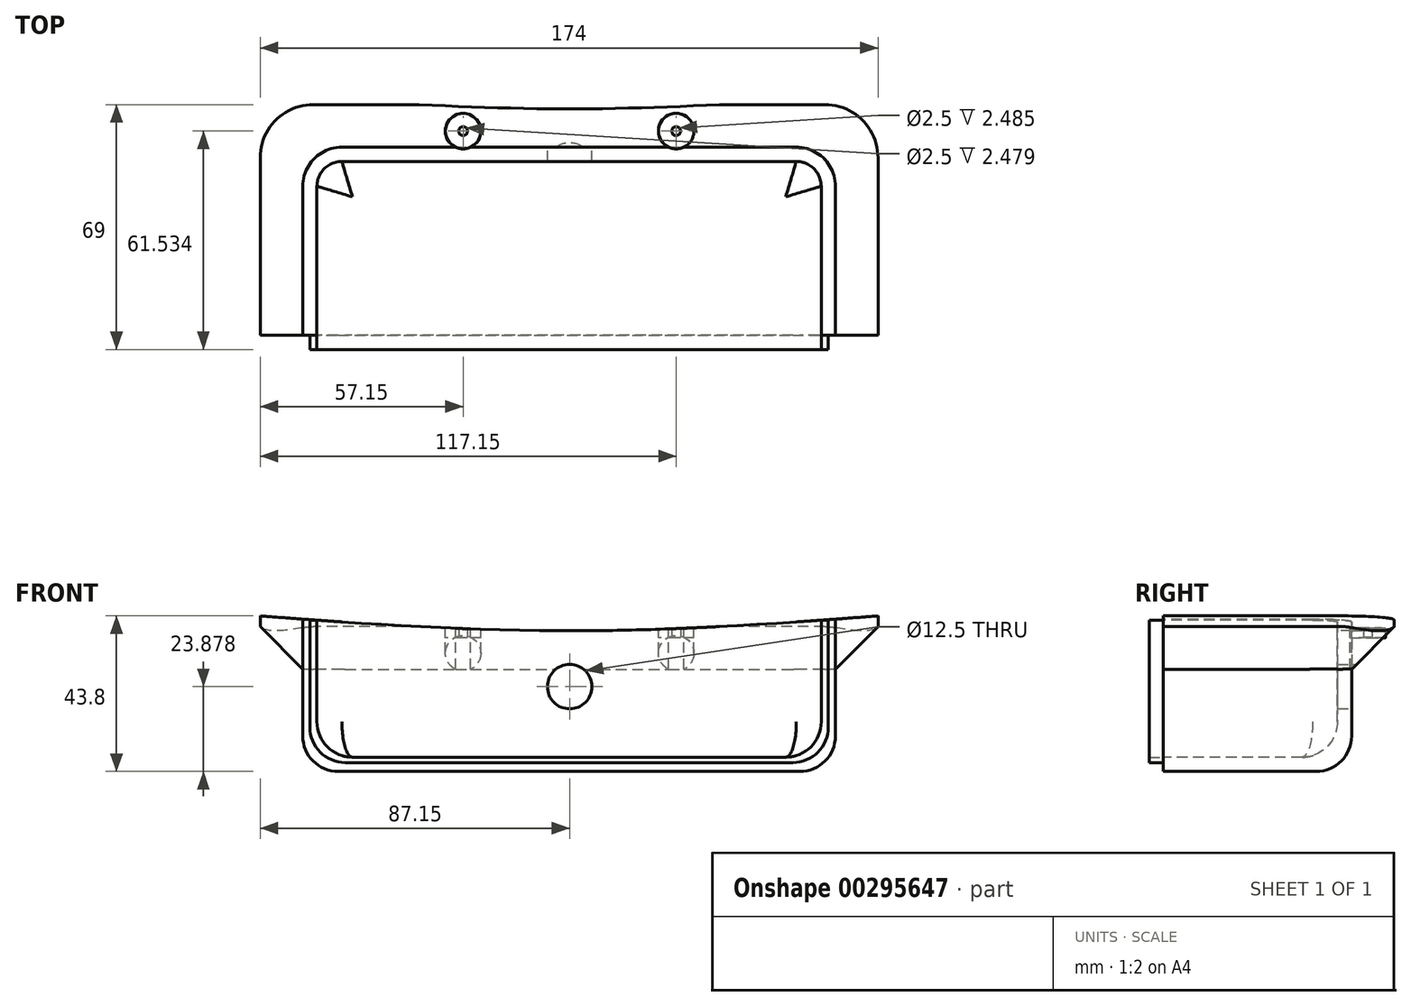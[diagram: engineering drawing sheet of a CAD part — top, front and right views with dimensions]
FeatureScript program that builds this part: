
annotation { "Feature Type Name" : "Feature", "Feature Type Description" : "" }
export const myFeature = defineFeature(function(context is Context, id is Id, definition is map)
    precondition{}
    {
        {
            var Q0;
            Q0=qCreatedBy(makeId("Top.planeOp"),FACE);
            var sketch = newSketch(context, id + "F0", { "sketchPlane" : qUnion([Q0])});
            skLineSegment(sketch, "E0.bottom", {"start": v(-64.15, 90.67) * mm, "end": v(63.85, 90.67) * mm});
            skLineSegment(sketch, "E0.top", {"start": v(-75.15, 37.67) * mm, "end": v(74.85, 37.67) * mm});
            skLineSegment(sketch, "E0.left", {"start": v(-75.15, 79.67) * mm, "end": v(-75.15, 37.67) * mm});
            skLineSegment(sketch, "E0.right", {"start": v(74.85, 79.67) * mm, "end": v(74.85, 37.67) * mm});
            skPoint(sketch, "E1.visualSharp", {"position": v(-75.15, 90.67) * mm});
            skArc(sketch, "E1.filletArc", {"start": v(-64.15, 90.67) * mm, "mid": v(-71.93, 87.45) * mm, "end": v(-75.15, 79.67) * mm});
            skPoint(sketch, "E2.visualSharp", {"position": v(74.85, 90.67) * mm});
            skArc(sketch, "E2.filletArc", {"start": v(74.85, 79.67) * mm, "mid": v(71.62, 87.45) * mm, "end": v(63.85, 90.67) * mm});
            skSolve(sketch);
        }
        {
            var Q0;
            Q0=qSketchRegion(id+"F0",true);
            extrude(context, id + "F1", {"entities" : qUnion([Q0]), "depth" : 43.8 * mm, "offsetDistance" : 25 * mm});
        }
        {
            var Q0;
            Q0=makeQuery(id+"F1.opExtrude","CAP_FACE",FACE,{"disambiguationData":[OSD([sQuery(id+"F0.wireOp",EDGE,"E0.bottom"),sQuery(id+"F0.wireOp",EDGE,"E0.top"),sQuery(id+"F0.wireOp",EDGE,"E0.left"),sQuery(id+"F0.wireOp",EDGE,"E0.right")])],"isStart":false});
            shell(context, id + "F2", {"entities" : qUnion([Q0]), "thickness" : 4 * mm});
        }
        {
            var Q0;
            Q0=makeQuery(id+"F1.opExtrude","CAP_FACE",FACE,{"disambiguationData":[OSD([sQuery(id+"F0.wireOp",EDGE,"E0.bottom"),sQuery(id+"F0.wireOp",EDGE,"E0.top"),sQuery(id+"F0.wireOp",EDGE,"E0.left"),sQuery(id+"F0.wireOp",EDGE,"E0.right"),sQuery(id+"F0.wireOp",EDGE,"E1.filletArc"),sQuery(id+"F0.wireOp",EDGE,"E2.filletArc")])],"isStart":false});
            var sketch = newSketch(context, id + "F3", { "sketchPlane" : qUnion([Q0])});
            skLineSegment(sketch, "E3.bottom", {"start": v(-71.15, 41.67) * mm, "end": v(70.85, 41.67) * mm});
            skLineSegment(sketch, "E3.top", {"start": v(-71.15, 37.67) * mm, "end": v(70.85, 37.67) * mm});
            skLineSegment(sketch, "E3.left", {"start": v(-71.15, 41.67) * mm, "end": v(-71.15, 37.67) * mm});
            skLineSegment(sketch, "E3.right", {"start": v(70.85, 41.67) * mm, "end": v(70.85, 37.67) * mm});
            skSolve(sketch);
        }
        {
            var Q0;
            Q0=qSketchRegion(id+"F3",true);
            extrude(context, id + "F4", {"entities" : qUnion([Q0]), "operationType" : NewBodyOperationType.REMOVE, "oppositeDirection" : true, "depth" : 39.8 * mm, "offsetDistance" : 25 * mm});
        }
        {
            var Q0;
            Q0=makeQuery(id+"FrwUbtnxUC9HyyJ_1.boolean.opBoolean","MERGE",FACE,{"derivedFrom":[makeQuery(id+"F1.opExtrude","CAP_FACE",FACE,{"disambiguationData":[OSD([sQuery(id+"F0.wireOp",EDGE,"E0.bottom"),sQuery(id+"F0.wireOp",EDGE,"E0.top"),sQuery(id+"F0.wireOp",EDGE,"E0.left"),sQuery(id+"F0.wireOp",EDGE,"E0.right"),sQuery(id+"F0.wireOp",EDGE,"E1.filletArc"),sQuery(id+"F0.wireOp",EDGE,"E2.filletArc")])],"isStart":false}),makeQuery(id+"FrwUbtnxUC9HyyJ_1.opExtrude","CAP_FACE",FACE,{"disambiguationData":[OSD([sQuery(id+"FibHU4dr98Ndzw2_1.wireOp",EDGE,"9rjzK8EU-co4c-AKP1-GJnL-XDDrkJgZbtAS.bottom"),sQuery(id+"FibHU4dr98Ndzw2_1.wireOp",EDGE,"9rjzK8EU-co4c-AKP1-GJnL-XDDrkJgZbtAS.top"),sQuery(id+"FibHU4dr98Ndzw2_1.wireOp",EDGE,"9rjzK8EU-co4c-AKP1-GJnL-XDDrkJgZbtAS.left"),sQuery(id+"FibHU4dr98Ndzw2_1.wireOp",EDGE,"9rjzK8EU-co4c-AKP1-GJnL-XDDrkJgZbtAS.right")])],"isStart":true})]});
            var sketch = newSketch(context, id + "F5", { "sketchPlane" : qUnion([Q0])});
            skLineSegment(sketch, "E4.top", {"start": v(74.85, 37.67) * mm, "end": v(86.85, 37.67) * mm});
            skPoint(sketch, "E5.visualSharp", {"position": v(86.85, 102.67) * mm});
            skLineSegment(sketch, "E6", {"start": v(86.85, 102.67) * mm, "end": v(86.85, 37.67) * mm});
            skLineSegment(sketch, "E7.bottom", {"start": v(-75.15, 37.67) * mm, "end": v(-87.15, 37.67) * mm});
            skLineSegment(sketch, "E8", {"start": v(86.85, 102.67) * mm, "end": v(-87.15, 102.67) * mm});
            skLineSegment(sketch, "E9", {"start": v(-87.15, 102.67) * mm, "end": v(-87.15, 37.67) * mm});
            skLineSegment(sketch, "E10", {"start": v(-75.15, 37.67) * mm, "end": v(-75.15, 79.67) * mm});
            skLineSegment(sketch, "E11", {"start": v(-75.15, 79.67) * mm, "end": v(-75.15, 79.67) * mm});
            skLineSegment(sketch, "E12", {"start": v(-64.15, 90.67) * mm, "end": v(-64.15, 90.67) * mm});
            skLineSegment(sketch, "E13", {"start": v(-64.15, 90.67) * mm, "end": v(63.85, 90.67) * mm});
            skLineSegment(sketch, "E14", {"start": v(63.85, 90.67) * mm, "end": v(63.85, 90.67) * mm});
            skLineSegment(sketch, "E15", {"start": v(74.85, 79.67) * mm, "end": v(74.85, 79.67) * mm});
            skLineSegment(sketch, "E16", {"start": v(74.85, 79.67) * mm, "end": v(74.85, 37.67) * mm});
            skPoint(sketch, "E17.visualSharp", {"position": v(-75.15, 90.67) * mm});
            skArc(sketch, "E17.filletArc", {"start": v(-64.15, 90.67) * mm, "mid": v(-71.93, 87.45) * mm, "end": v(-75.15, 79.67) * mm});
            skPoint(sketch, "E18.visualSharp", {"position": v(74.85, 90.67) * mm});
            skArc(sketch, "E18.filletArc", {"start": v(74.85, 79.67) * mm, "mid": v(71.62, 87.45) * mm, "end": v(63.85, 90.67) * mm});
            skSolve(sketch);
        }
        {
            var Q0;
            Q0=qSketchRegion(id+"F5",true);
            extrude(context, id + "F6", {"entities" : qUnion([Q0]), "oppositeDirection" : true, "depth" : 15 * mm});
        }
        {
            var Q0;
            Q0=makeQuery(id+"F6.opExtrude","CAP_EDGE",EDGE,{"disambiguationData":[OSD([sQuery(id+"F5.wireOp",EDGE,"OsvB9Zjt-Pbkl-vpw5-N01A-Guk8HrNlOFjG")])],"isStart":false});
            var Q1;
            Q1=makeQuery(id+"F6.opExtrude","CAP_EDGE",EDGE,{"disambiguationData":[OSD([sQuery(id+"F5.wireOp",EDGE,"jzA2utPZ-bsNO-buFr-XQbU-ETDa1rF8MsZR")])],"isStart":false});
            var Q2;
            Q2=makeQuery(id+"F6.opExtrude","CAP_EDGE",EDGE,{"disambiguationData":[OSD([sQuery(id+"F5.wireOp",EDGE,"E6")])],"isStart":false});
            var Q3;
            Q3=makeQuery(id+"F6.opExtrude","CAP_EDGE",EDGE,{"disambiguationData":[OSD([sQuery(id+"F5.wireOp",EDGE,"ZfQyCJF3-zcwV-7PIL-13Iy-nZyDA9thB6iG")])],"isStart":false});
            var Q4;
            Q4=makeQuery(id+"F6.opExtrude","CAP_EDGE",EDGE,{"disambiguationData":[OSD([sQuery(id+"F5.wireOp",EDGE,"E8")])],"isStart":false});
            var Q5;
            Q5=makeQuery(id+"F6.opExtrude","CAP_EDGE",EDGE,{"disambiguationData":[OSD([sQuery(id+"F5.wireOp",EDGE,"E9")])],"isStart":false});
            chamfer(context, id + "F7", {"entities" : qUnion([Q0, Q1, Q2, Q3, Q4, Q5]), "width" : 12 * mm, "tangentPropagation" : true});
        }
        {
            var Q0;
            Q0=makeQuery(id+"F6.opExtrude","SWEPT_EDGE",EDGE,{"disambiguationData":[OSD([sQuery(id+"F5.wireOp",EDGE,"E8"),sQuery(id+"F5.wireOp",EDGE,"E9")])]});
            var Q1;
            Q1=makeQuery(id+"F6.opExtrude","SWEPT_EDGE",EDGE,{"disambiguationData":[OSD([sQuery(id+"F5.wireOp",EDGE,"E6"),sQuery(id+"F5.wireOp",EDGE,"E8")])]});
            fillet(context, id + "F8", {"entities" : qUnion([Q0, Q1]), "radius" : 15 * mm, "tangentPropagation" : true, "allowEdgeOverflow" : false});
        }
        {
            var Q0;
            Q0=makeQuery(id+"F7.opChamfer","BLEND_EDGE",EDGE,{"blendedFrom":[makeQuery(id+"F6.opExtrude","CAP_EDGE",EDGE,{"disambiguationData":[OSD([sQuery(id+"F5.wireOp",EDGE,"E6")])],"isStart":false}),makeQuery(id+"F6.opExtrude","CAP_EDGE",EDGE,{"disambiguationData":[OSD([sQuery(id+"F5.wireOp",EDGE,"E8")])],"isStart":false})],"blendedInto":[]});
            var Q1;
            Q1=makeQuery(id+"F7.opChamfer","BLEND_EDGE",EDGE,{"blendedFrom":[makeQuery(id+"F6.opExtrude","CAP_EDGE",EDGE,{"disambiguationData":[OSD([sQuery(id+"F5.wireOp",EDGE,"E8")])],"isStart":false}),makeQuery(id+"F6.opExtrude","CAP_EDGE",EDGE,{"disambiguationData":[OSD([sQuery(id+"F5.wireOp",EDGE,"E9")])],"isStart":false})],"blendedInto":[]});
            fillet(context, id + "F9", {"entities" : qUnion([Q0, Q1]), "radius" : 17 * mm, "tangentPropagation" : true, "allowEdgeOverflow" : false});
        }
        {
            var Q0;
            {var subQ0=sQuery(id+"F5.wireOp",EDGE,"E13");var subQ1=sQuery(id+"F5.wireOp",EDGE,"E8");var subQ2=sQuery(id+"F5.wireOp",EDGE,"E6");var subQ3=sQuery(id+"F5.wireOp",EDGE,"E4.top");var subQ4=sQuery(id+"F5.wireOp",EDGE,"E18.filletArc");var subQ5=sQuery(id+"F5.wireOp",EDGE,"E16");Q0=makeQuery(id+"FgmOIsl14va52HR_2.boolean.opBoolean","SPLIT",FACE,{"disambiguationData":[TD([makeQuery(id+"F6.opExtrude","SWEPT_FACE",FACE,{"disambiguationData":[OSD([subQ3])]})])],"derivedFrom":makeQuery(id+"Fe1wAfX2hFDYVoF_2.boolean.opBoolean","MERGE",FACE,{"derivedFrom":[makeQuery(id+"F6.opExtrude","CAP_FACE",FACE,{"disambiguationData":[OSD([subQ3,subQ2,sQuery(id+"F5.wireOp",EDGE,"E7.bottom"),subQ1,sQuery(id+"F5.wireOp",EDGE,"E9"),sQuery(id+"F5.wireOp",EDGE,"E10"),subQ0,subQ5,sQuery(id+"F5.wireOp",EDGE,"E17.filletArc"),subQ4])],"isStart":true}),makeQuery(id+"Fe1wAfX2hFDYVoF_2.opExtrude","CAP_FACE",FACE,{"disambiguationData":[OSD([sQuery(id+"Fb9MMb573N5PaO1_2.wireOp",EDGE,"NLJTObmN-SUbK-zKRp-w8bl-v2nN1BY6rHCR")])],"isStart":true}),makeQuery(id+"Fe1wAfX2hFDYVoF_2.opExtrude","CAP_FACE",FACE,{"disambiguationData":[OSD([sQuery(id+"Fb9MMb573N5PaO1_2.wireOp",EDGE,"s3ml98qp-wij4-XS56-vTp4-YSEt5g6wRKUZ")])],"isStart":true}),makeQuery(id+"Fe1wAfX2hFDYVoF_2.opExtrude","CAP_FACE",FACE,{"disambiguationData":[OSD([sQuery(id+"Fb9MMb573N5PaO1_2.wireOp",EDGE,"b1kLfqmR-9x7Y-TcUW-Umgw-XTBiy1vxkqET")])],"isStart":true}),makeQuery(id+"Fe1wAfX2hFDYVoF_2.opExtrude","CAP_FACE",FACE,{"disambiguationData":[OSD([sQuery(id+"Fb9MMb573N5PaO1_2.wireOp",EDGE,"wZv8IqiW-lJnz-yde2-UiWY-uM58CcvMkqUG")])],"isStart":true})]})});}
            var sketch = newSketch(context, id + "F10", { "sketchPlane" : qUnion([Q0])});
            skCircle(sketch, "E19", {"center": v(30, 95.2) * mm, "radius": 5 * mm});
            skCircle(sketch, "E20", {"center": v(-30, 95.2) * mm, "radius": 5 * mm});
            skSolve(sketch);
        }
        {
            var Q0;
            Q0=qSketchRegion(id+"F10",true);
            extrude(context, id + "F11", {"entities" : qUnion([Q0]), "operationType" : NewBodyOperationType.REMOVE, "oppositeDirection" : true, "depth" : 15 * mm});
        }
        {
            var Q0;
            {var subQ0=sQuery(id+"F5.wireOp",EDGE,"E13");var subQ1=sQuery(id+"F5.wireOp",EDGE,"E8");var subQ2=sQuery(id+"F5.wireOp",EDGE,"E6");var subQ3=sQuery(id+"F5.wireOp",EDGE,"E4.top");var subQ4=sQuery(id+"F5.wireOp",EDGE,"E18.filletArc");var subQ5=sQuery(id+"F5.wireOp",EDGE,"E16");Q0=makeQuery(id+"FgmOIsl14va52HR_2.boolean.opBoolean","SPLIT",FACE,{"disambiguationData":[TD([makeQuery(id+"F6.opExtrude","SWEPT_FACE",FACE,{"disambiguationData":[OSD([subQ3])]})])],"derivedFrom":makeQuery(id+"Fe1wAfX2hFDYVoF_2.boolean.opBoolean","MERGE",FACE,{"derivedFrom":[makeQuery(id+"F6.opExtrude","CAP_FACE",FACE,{"disambiguationData":[OSD([subQ3,subQ2,sQuery(id+"F5.wireOp",EDGE,"E7.bottom"),subQ1,sQuery(id+"F5.wireOp",EDGE,"E9"),sQuery(id+"F5.wireOp",EDGE,"E10"),subQ0,subQ5,sQuery(id+"F5.wireOp",EDGE,"E17.filletArc"),subQ4])],"isStart":true}),makeQuery(id+"Fe1wAfX2hFDYVoF_2.opExtrude","CAP_FACE",FACE,{"disambiguationData":[OSD([sQuery(id+"Fb9MMb573N5PaO1_2.wireOp",EDGE,"NLJTObmN-SUbK-zKRp-w8bl-v2nN1BY6rHCR")])],"isStart":true}),makeQuery(id+"Fe1wAfX2hFDYVoF_2.opExtrude","CAP_FACE",FACE,{"disambiguationData":[OSD([sQuery(id+"Fb9MMb573N5PaO1_2.wireOp",EDGE,"s3ml98qp-wij4-XS56-vTp4-YSEt5g6wRKUZ")])],"isStart":true}),makeQuery(id+"Fe1wAfX2hFDYVoF_2.opExtrude","CAP_FACE",FACE,{"disambiguationData":[OSD([sQuery(id+"Fb9MMb573N5PaO1_2.wireOp",EDGE,"b1kLfqmR-9x7Y-TcUW-Umgw-XTBiy1vxkqET")])],"isStart":true}),makeQuery(id+"Fe1wAfX2hFDYVoF_2.opExtrude","CAP_FACE",FACE,{"disambiguationData":[OSD([sQuery(id+"Fb9MMb573N5PaO1_2.wireOp",EDGE,"wZv8IqiW-lJnz-yde2-UiWY-uM58CcvMkqUG")])],"isStart":true})]})});}
            var sketch = newSketch(context, id + "F12", { "sketchPlane" : qUnion([Q0])});
            skCircle(sketch, "E21", {"center": v(-30, 95.2) * mm, "radius": 5 * mm});
            skCircle(sketch, "E22", {"center": v(30, 95.2) * mm, "radius": 5 * mm});
            skSolve(sketch);
        }
        {
            var Q0;
            Q0=qSketchRegion(id+"F12",true);
            extrude(context, id + "F13", {"entities" : qUnion([Q0]), "oppositeDirection" : true, "depth" : 6.2 * mm});
        }
        {
            var Q0;
            Q0=makeQuery(id+"F6.opExtrude","SWEPT_FACE",FACE,{"disambiguationData":[OSD([sQuery(id+"F5.wireOp",EDGE,"E7.bottom")])]});
            var sketch = newSketch(context, id + "F14", { "sketchPlane" : qUnion([Q0])});
            skFitSpline(sketch, "E23", {"points": [v(-87.15, 43.8) * mm, v(0, 39.6) * mm, v(86.85, 43.8) * mm], "startDerivative": vector(174.23, -13.41) * mm, "endDerivative": vector(173.77, 13.42) * mm});
            skLineSegment(sketch, "E24", {"start": v(86.85, 43.8) * mm, "end": v(-87.15, 43.8) * mm});
            skSolve(sketch);
        }
        {
            var Q0;
            Q0=qSketchRegion(id+"F14",true);
            extrude(context, id + "F15", {"entities" : qUnion([Q0]), "operationType" : NewBodyOperationType.REMOVE, "oppositeDirection" : true, "depth" : 70 * mm});
        }
        {
            var Q0;
            Q0=makeQuery(id+"F13.opExtrude","CAP_FACE",FACE,{"disambiguationData":[OSD([sQuery(id+"F12.wireOp",EDGE,"E21")])],"isStart":false});
            var sketch = newSketch(context, id + "F16", { "sketchPlane" : qUnion([Q0])});
            skCircle(sketch, "E25", {"center": v(-30, -95.2) * mm, "radius": 1.25 * mm});
            skSolve(sketch);
        }
        {
            var Q0;
            Q0=qSketchRegion(id+"F16",true);
            extrude(context, id + "F17", {"entities" : qUnion([Q0]), "operationType" : NewBodyOperationType.REMOVE, "oppositeDirection" : true, "depth" : 3 * mm, "offsetDistance" : 25 * mm});
        }
        {
            var Q0;
            Q0=makeQuery(id+"F1.opExtrude","CAP_EDGE",EDGE,{"disambiguationData":[OSD([sQuery(id+"F0.wireOp",EDGE,"E0.right")])],"isStart":true});
            var Q1;
            Q1=makeQuery(id+"F1.opExtrude","CAP_EDGE",EDGE,{"disambiguationData":[OSD([sQuery(id+"F0.wireOp",EDGE,"E0.bottom")])],"isStart":true});
            var Q2;
            Q2=makeQuery(id+"F1.opExtrude","CAP_EDGE",EDGE,{"disambiguationData":[OSD([sQuery(id+"F0.wireOp",EDGE,"E2.filletArc")])],"isStart":true});
            var Q3;
            Q3=makeQuery(id+"F1.opExtrude","CAP_EDGE",EDGE,{"disambiguationData":[OSD([sQuery(id+"F0.wireOp",EDGE,"E1.filletArc")])],"isStart":true});
            var Q4;
            Q4=makeQuery(id+"F1.opExtrude","CAP_EDGE",EDGE,{"disambiguationData":[OSD([sQuery(id+"F0.wireOp",EDGE,"E0.left")])],"isStart":true});
            fillet(context, id + "F18", {"entities" : qUnion([Q0, Q1, Q2, Q3, Q4]), "radius" : 10 * mm, "tangentPropagation" : true, "allowEdgeOverflow" : false});
        }
        {
            var Q0;
            {var subQ0=sQuery(id+"F0.wireOp",EDGE,"E0.left");Q0=makeQuery(id+"F4.boolean.opBoolean","MERGE",EDGE,{"derivedFrom":[makeQuery(id+"F2.opShell","OFFSET_EDGE",EDGE,{"disambiguationData":[OSD([subQ0]),TDD([makeQuery(id+"F1.opExtrude","CAP_EDGE",EDGE,{"disambiguationData":[OSD([subQ0])],"isStart":true})])]}),makeQuery(id+"F4.opExtrude","CAP_EDGE",EDGE,{"disambiguationData":[OSD([sQuery(id+"F3.wireOp",EDGE,"E3.left")])],"isStart":false})]});}
            var Q1;
            {var subQ0=sQuery(id+"F0.wireOp",EDGE,"E1.filletArc");Q1=makeQuery(id+"F2.opShell","OFFSET_EDGE",EDGE,{"disambiguationData":[OSD([subQ0]),TDD([makeQuery(id+"F1.opExtrude","CAP_EDGE",EDGE,{"disambiguationData":[OSD([subQ0])],"isStart":true})])]});}
            var Q2;
            {var subQ0=sQuery(id+"F0.wireOp",EDGE,"E0.bottom");Q2=makeQuery(id+"F2.opShell","OFFSET_EDGE",EDGE,{"disambiguationData":[OSD([subQ0]),TDD([makeQuery(id+"F1.opExtrude","CAP_EDGE",EDGE,{"disambiguationData":[OSD([subQ0])],"isStart":true})])]});}
            var Q3;
            {var subQ0=sQuery(id+"F0.wireOp",EDGE,"E2.filletArc");Q3=makeQuery(id+"F2.opShell","OFFSET_EDGE",EDGE,{"disambiguationData":[OSD([subQ0]),TDD([makeQuery(id+"F1.opExtrude","CAP_EDGE",EDGE,{"disambiguationData":[OSD([subQ0])],"isStart":true})])]});}
            var Q4;
            {var subQ0=sQuery(id+"F0.wireOp",EDGE,"E0.right");Q4=makeQuery(id+"F4.boolean.opBoolean","MERGE",EDGE,{"derivedFrom":[makeQuery(id+"F2.opShell","OFFSET_EDGE",EDGE,{"disambiguationData":[OSD([subQ0]),TDD([makeQuery(id+"F1.opExtrude","CAP_EDGE",EDGE,{"disambiguationData":[OSD([subQ0])],"isStart":true})])]}),makeQuery(id+"F4.opExtrude","CAP_EDGE",EDGE,{"disambiguationData":[OSD([sQuery(id+"F3.wireOp",EDGE,"E3.right")])],"isStart":false})]});}
            fillet(context, id + "F19", {"entities" : qUnion([Q0, Q1, Q2, Q3, Q4]), "radius" : 10 * mm, "tangentPropagation" : true, "allowEdgeOverflow" : false});
        }
        {
            var Q0;
            Q0=makeQuery(id+"F1.opExtrude","SWEPT_FACE",FACE,{"disambiguationData":[OSD([sQuery(id+"F0.wireOp",EDGE,"E0.bottom")])]});
            var sketch = newSketch(context, id + "F20", { "sketchPlane" : qUnion([Q0])});
            skCircle(sketch, "E26", {"center": v(0, 23.88) * mm, "radius": 6.25 * mm});
            skSolve(sketch);
        }
        {
            var Q0;
            Q0 = qSketchRegion(id + "F20", true);
            extrude(context, id + "F21", {"entities" : qUnion([Q0]), "operationType" : NewBodyOperationType.REMOVE, "endBound" : BoundingType.SYMMETRIC, "oppositeDirection" : true, "depth" : 10 * mm, "offsetDistance" : 25 * mm});
        }
        {
            var Q0;
            Q0=makeQuery(id+"F13.opExtrude","CAP_FACE",FACE,{"disambiguationData":[OSD([sQuery(id+"F12.wireOp",EDGE,"E21")])],"isStart":false});
            var sketch = newSketch(context, id + "F22", { "sketchPlane" : qUnion([Q0])});
            skCircle(sketch, "E27", {"center": v(-30, -95.2) * mm, "radius": 1.25 * mm});
            skSolve(sketch);
        }
        {
            var Q0;
            Q0 = qSketchRegion(id + "F22", true);
            extrude(context, id + "F23", {"entities" : qUnion([Q0]), "operationType" : NewBodyOperationType.ADD, "oppositeDirection" : true, "depth" : .2 * mm, "offsetDistance" : 25 * mm});
        }
        {
            var Q0;
            Q0=makeQuery(id+"F13.opExtrude","CAP_FACE",FACE,{"disambiguationData":[OSD([sQuery(id+"F12.wireOp",EDGE,"E22")])],"isStart":false});
            var sketch = newSketch(context, id + "F24", { "sketchPlane" : qUnion([Q0])});
            skCircle(sketch, "E28", {"center": v(30, -95.2) * mm, "radius": 1.25 * mm});
            skSolve(sketch);
        }
        {
            var Q0;
            Q0 = qSketchRegion(id + "F24", true);
            extrude(context, id + "F25", {"entities" : qUnion([Q0]), "operationType" : NewBodyOperationType.REMOVE, "oppositeDirection" : true, "depth" : 3 * mm, "offsetDistance" : 25 * mm});
        }
        {
            var Q0;
            Q0=makeQuery(id+"F13.opExtrude","CAP_FACE",FACE,{"disambiguationData":[OSD([sQuery(id+"F12.wireOp",EDGE,"E22")])],"isStart":false});
            var sketch = newSketch(context, id + "F26", { "sketchPlane" : qUnion([Q0])});
            skCircle(sketch, "E29", {"center": v(30, -95.2) * mm, "radius": 1.25 * mm});
            skSolve(sketch);
        }
        {
            var Q0;
            Q0 = qSketchRegion(id + "F26", true);
            extrude(context, id + "F27", {"entities" : qUnion([Q0]), "operationType" : NewBodyOperationType.ADD, "oppositeDirection" : true, "depth" : 0.2 * mm, "offsetDistance" : 25 * mm});
        }
        {
            var Q0;
            Q0=makeQuery(id+"F1.opExtrude","SWEPT_FACE",FACE,{"disambiguationData":[OSD([sQuery(id+"F0.wireOp",EDGE,"E0.top")])]});
            var sketch = newSketch(context, id + "F28", { "sketchPlane" : qUnion([Q0])});
            skLineSegment(sketch, "E30.bottom", {"start": v(-71.15, 42.63) * mm, "end": v(-73.15, 42.63) * mm});
            skLineSegment(sketch, "E30.left", {"start": v(-71.15, 42.63) * mm, "end": v(-71.15, 14) * mm});
            skLineSegment(sketch, "E30.right", {"start": v(-73.15, 42.63) * mm, "end": v(-73.15, 12.5) * mm});
            skLineSegment(sketch, "E31.bottom", {"start": v(60.85, 4) * mm, "end": v(-61.15, 4) * mm});
            skLineSegment(sketch, "E31.top", {"start": v(62.85, 2.5) * mm, "end": v(-63.15, 2.5) * mm});
            skLineSegment(sketch, "E32.bottom", {"start": v(70.85, 42.6) * mm, "end": v(72.85, 42.6) * mm});
            skArc(sketch, "E33.filletArc", {"start": v(-71.15, 14) * mm, "mid": v(-68.22, 6.93) * mm, "end": v(-61.15, 4) * mm});
            skArc(sketch, "E34.filletArc", {"start": v(-73.15, 12.5) * mm, "mid": v(-70.22, 5.43) * mm, "end": v(-63.15, 2.5) * mm});
            skLineSegment(sketch, "E35.top", {"start": v(72.85, 42.6) * mm, "end": v(70.85, 42.6) * mm});
            skLineSegment(sketch, "E35.left", {"start": v(72.85, 12.5) * mm, "end": v(72.85, 42.6) * mm});
            skLineSegment(sketch, "E35.right", {"start": v(70.85, 14) * mm, "end": v(70.85, 42.6) * mm});
            skArc(sketch, "E36.filletArc", {"start": v(60.85, 4) * mm, "mid": v(67.92, 6.93) * mm, "end": v(70.85, 14) * mm});
            skArc(sketch, "E37.filletArc", {"start": v(62.85, 2.5) * mm, "mid": v(69.92, 5.43) * mm, "end": v(72.85, 12.5) * mm});
            skSolve(sketch);
        }
        {
            var Q0;
            Q0 = qSketchRegion(id + "F28", true);
            extrude(context, id + "F29", {"entities" : qUnion([Q0]), "operationType" : NewBodyOperationType.ADD, "depth" : 4 * mm, "offsetDistance" : 25 * mm});
        }
    });
